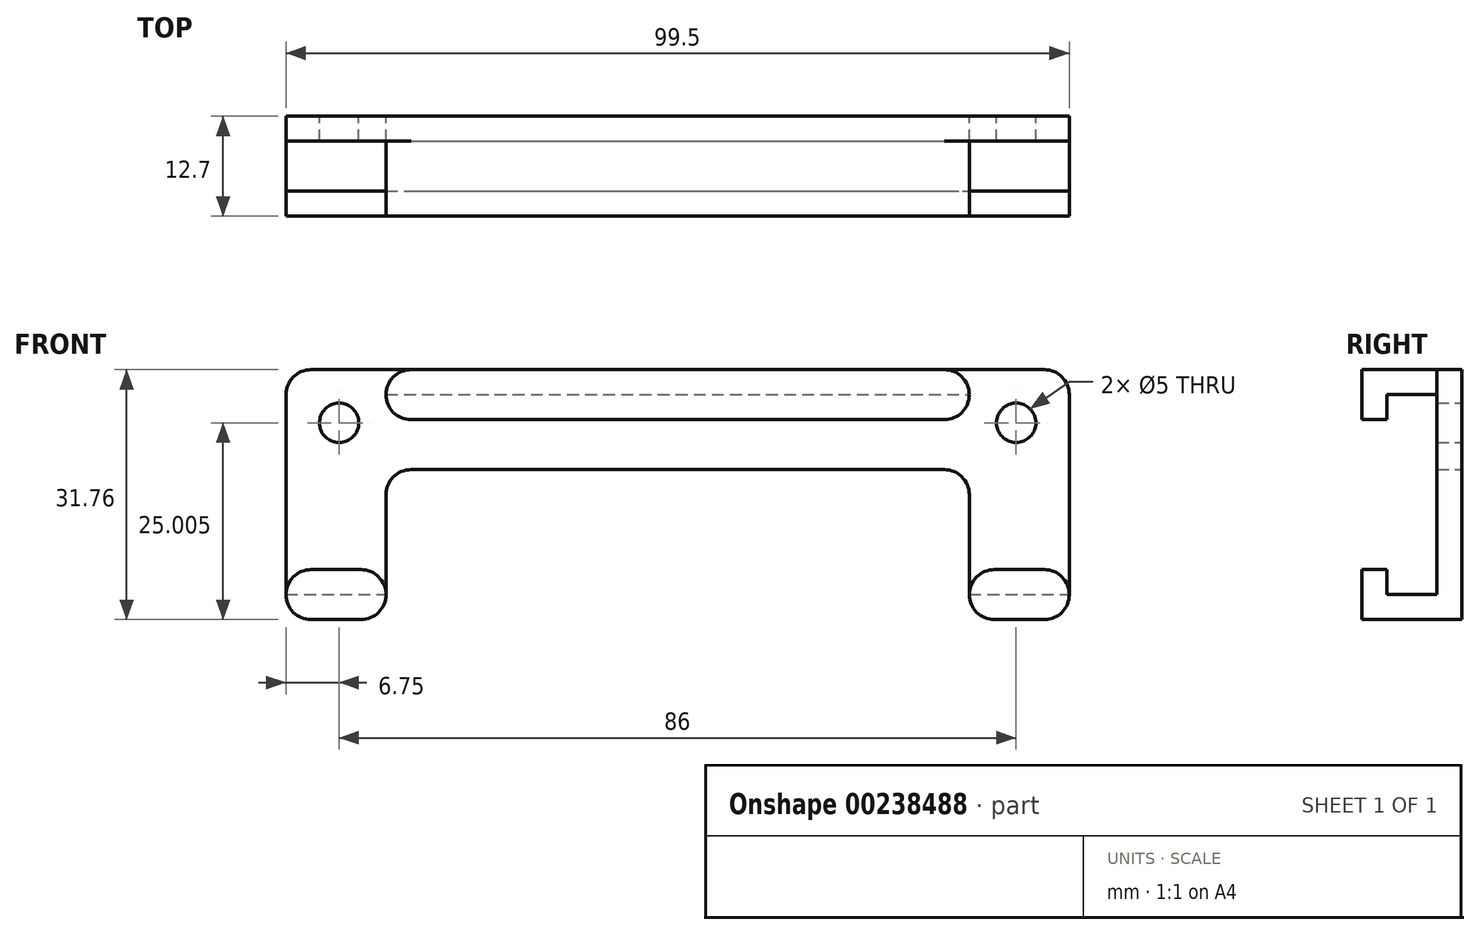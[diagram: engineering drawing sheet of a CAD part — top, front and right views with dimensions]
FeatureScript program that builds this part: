
annotation { "Feature Type Name" : "Feature", "Feature Type Description" : "" }
export const myFeature = defineFeature(function(context is Context, id is Id, definition is map)
    precondition{}
    {
        {
            var Q0;
            Q0=qCreatedBy(makeId("Front.planeOp"),FACE);
            var sketch = newSketch(context, id + "F0", { "sketchPlane" : qUnion([Q0])});
            skLineSegment(sketch, "E0.bottom", {"start": v(49.75, 15.88) * mm, "end": v(-49.75, 15.88) * mm});
            skLineSegment(sketch, "E0.left", {"start": v(49.75, 15.88) * mm, "end": v(49.75, -15.88) * mm});
            skLineSegment(sketch, "E0.right", {"start": v(-49.75, 15.88) * mm, "end": v(-49.75, -15.88) * mm});
            skPoint(sketch, "E0.middle", {"position": v(0, 0) * mm});
            skLineSegment(sketch, "E1.top", {"start": v(-49.75, 9.13) * mm, "end": v(-43, 9.13) * mm, "construction": true});
            skLineSegment(sketch, "E1.right", {"start": v(-43, 15.87) * mm, "end": v(-43, 9.13) * mm, "construction": true});
            skLineSegment(sketch, "E2.top", {"start": v(49.75, 9.13) * mm, "end": v(43, 9.13) * mm, "construction": true});
            skLineSegment(sketch, "E2.right", {"start": v(43, 15.88) * mm, "end": v(43, 9.13) * mm, "construction": true});
            skCircle(sketch, "E3", {"center": v(-43, 9.13) * mm, "radius": 2.5 * mm});
            skCircle(sketch, "E4", {"center": v(43, 9.13) * mm, "radius": 2.5 * mm});
            skLineSegment(sketch, "E5", {"start": v(-37.05, 3.17) * mm, "end": v(37.05, 3.17) * mm});
            skLineSegment(sketch, "E6", {"start": v(37.05, 3.17) * mm, "end": v(37.05, -15.88) * mm});
            skLineSegment(sketch, "E7", {"start": v(-37.05, 3.17) * mm, "end": v(-37.05, -15.88) * mm});
            skLineSegment(sketch, "E8", {"start": v(-37.05, -15.88) * mm, "end": v(-49.75, -15.88) * mm});
            skLineSegment(sketch, "E9", {"start": v(37.05, -15.88) * mm, "end": v(49.75, -15.87) * mm});
            skSolve(sketch);
        }
        {
            var Q0;
            Q0=makeQuery(id+"F0.imprint","IMPRINT",FACE,{"disambiguationData":[TD([[makeQuery(id+"F0.imprint","IMPRINT",EDGE,{"derivedFrom":sQuery(id+"F0.wireOp",EDGE,"E0.bottom")}),1.0]])]});
            extrude(context, id + "F1", {"entities" : qUnion([Q0]), "depth" : 3.17 * mm});
        }
        {
            var Q0;
            Q0=makeQuery(id+"F1.opExtrude","CAP_FACE",FACE,{"disambiguationData":[OSD([sQuery(id+"F0.wireOp",EDGE,"E0.bottom"),sQuery(id+"F0.wireOp",EDGE,"E0.left"),sQuery(id+"F0.wireOp",EDGE,"E0.right"),sQuery(id+"F0.wireOp",EDGE,"E3"),sQuery(id+"F0.wireOp",EDGE,"E4"),sQuery(id+"F0.wireOp",EDGE,"E5"),sQuery(id+"F0.wireOp",EDGE,"E6"),sQuery(id+"F0.wireOp",EDGE,"E7"),sQuery(id+"F0.wireOp",EDGE,"E8"),sQuery(id+"F0.wireOp",EDGE,"E9")])],"isStart":false});
            var sketch = newSketch(context, id + "F2", { "sketchPlane" : qUnion([Q0])});
            skLineSegment(sketch, "E10.bottom", {"start": v(-49.75, -15.88) * mm, "end": v(-37.05, -15.88) * mm});
            skLineSegment(sketch, "E10.top", {"start": v(-49.75, -12.7) * mm, "end": v(-37.05, -12.7) * mm});
            skLineSegment(sketch, "E10.left", {"start": v(-49.75, -15.88) * mm, "end": v(-49.75, -12.7) * mm});
            skLineSegment(sketch, "E10.right", {"start": v(-37.05, -15.88) * mm, "end": v(-37.05, -12.7) * mm});
            skLineSegment(sketch, "E11.bottom", {"start": v(37.05, -15.88) * mm, "end": v(49.75, -15.88) * mm});
            skLineSegment(sketch, "E11.top", {"start": v(37.05, -12.7) * mm, "end": v(49.75, -12.7) * mm});
            skLineSegment(sketch, "E11.left", {"start": v(37.05, -15.88) * mm, "end": v(37.05, -12.7) * mm});
            skLineSegment(sketch, "E11.right", {"start": v(49.75, -15.88) * mm, "end": v(49.75, -12.7) * mm});
            skLineSegment(sketch, "E12.bottom", {"start": v(-49.75, 15.88) * mm, "end": v(49.75, 15.88) * mm});
            skLineSegment(sketch, "E12.left", {"start": v(-49.75, 15.88) * mm, "end": v(-49.75, 12.7) * mm});
            skLineSegment(sketch, "E12.right", {"start": v(49.75, 15.88) * mm, "end": v(49.75, 12.7) * mm});
            skLineSegment(sketch, "E13", {"start": v(-37.05, 3.17) * mm, "end": v(-37.05, 15.88) * mm, "construction": true});
            skLineSegment(sketch, "E14", {"start": v(-49.75, 12.7) * mm, "end": v(-37.05, 12.7) * mm, "construction": true});
            skLineSegment(sketch, "E15", {"start": v(37.05, 3.17) * mm, "end": v(37.05, 15.88) * mm, "construction": true});
            skLineSegment(sketch, "E16", {"start": v(49.75, 12.7) * mm, "end": v(37.05, 12.7) * mm, "construction": true});
            skLineSegment(sketch, "E17.bottom", {"start": v(-37.05, 15.88) * mm, "end": v(37.05, 15.88) * mm});
            skLineSegment(sketch, "E17.top", {"start": v(-37.05, 12.7) * mm, "end": v(37.05, 12.7) * mm});
            skLineSegment(sketch, "E17.left", {"start": v(-37.05, 15.88) * mm, "end": v(-37.05, 12.7) * mm});
            skLineSegment(sketch, "E17.right", {"start": v(37.05, 15.88) * mm, "end": v(37.05, 12.7) * mm});
            skSolve(sketch);
        }
        {
            var Q0;
            Q0 = qSketchRegion(id + "F2", true);
            extrude(context, id + "F3", {"entities" : qUnion([Q0]), "operationType" : NewBodyOperationType.ADD, "depth" : 9.52 * mm});
        }
        {
            var Q0;
            Q0=makeQuery(id+"F3.opExtrude","SWEPT_FACE",FACE,{"disambiguationData":[OSD([sQuery(id+"F2.wireOp",EDGE,"E11.top")])]});
            var sketch = newSketch(context, id + "F4", { "sketchPlane" : qUnion([Q0])});
            skLineSegment(sketch, "E18.bottom", {"start": v(-49.75, -12.7) * mm, "end": v(-37.05, -12.7) * mm});
            skLineSegment(sketch, "E18.top", {"start": v(-49.75, -9.53) * mm, "end": v(-37.05, -9.53) * mm});
            skLineSegment(sketch, "E18.left", {"start": v(-49.75, -12.7) * mm, "end": v(-49.75, -9.53) * mm});
            skLineSegment(sketch, "E18.right", {"start": v(-37.05, -12.7) * mm, "end": v(-37.05, -9.53) * mm});
            skLineSegment(sketch, "E19.bottom", {"start": v(49.75, -12.7) * mm, "end": v(37.05, -12.7) * mm});
            skLineSegment(sketch, "E19.top", {"start": v(49.75, -9.53) * mm, "end": v(37.05, -9.53) * mm});
            skLineSegment(sketch, "E19.left", {"start": v(49.75, -12.7) * mm, "end": v(49.75, -9.53) * mm});
            skLineSegment(sketch, "E19.right", {"start": v(37.05, -12.7) * mm, "end": v(37.05, -9.53) * mm});
            skSolve(sketch);
        }
        {
            var Q0;
            Q0 = qSketchRegion(id + "F4", true);
            extrude(context, id + "F5", {"entities" : qUnion([Q0]), "operationType" : NewBodyOperationType.ADD, "depth" : 3.17 * mm});
        }
        {
            var Q0;
            Q0=makeQuery(id+"F3.opExtrude","SWEPT_FACE",FACE,{"disambiguationData":[OSD([sQuery(id+"F2.wireOp",EDGE,"E17.top")])]});
            var sketch = newSketch(context, id + "F6", { "sketchPlane" : qUnion([Q0])});
            skLineSegment(sketch, "E20.bottom", {"start": v(-37.05, 12.7) * mm, "end": v(37.05, 12.7) * mm});
            skLineSegment(sketch, "E20.top", {"start": v(-37.05, 9.53) * mm, "end": v(37.05, 9.53) * mm});
            skLineSegment(sketch, "E20.left", {"start": v(-37.05, 12.7) * mm, "end": v(-37.05, 9.53) * mm});
            skLineSegment(sketch, "E20.right", {"start": v(37.05, 12.7) * mm, "end": v(37.05, 9.53) * mm});
            skSolve(sketch);
        }
        {
            var Q0;
            Q0 = qSketchRegion(id + "F6", true);
            extrude(context, id + "F7", {"entities" : qUnion([Q0]), "operationType" : NewBodyOperationType.ADD, "depth" : 3.17 * mm});
        }
        {
            var Q0;
            Q0=makeQuery(id+"F1.opExtrude","SWEPT_EDGE",EDGE,{"disambiguationData":[OSD([sQuery(id+"F0.wireOp",EDGE,"E0.bottom"),sQuery(id+"F0.wireOp",EDGE,"E0.right")])]});
            var Q1;
            Q1=makeQuery(id+"F3.boolean.opBoolean","MERGE",EDGE,{"derivedFrom":[makeQuery(id+"F1.opExtrude","SWEPT_EDGE",EDGE,{"disambiguationData":[OSD([sQuery(id+"F0.wireOp",EDGE,"E0.right"),sQuery(id+"F0.wireOp",EDGE,"E8")])]}),makeQuery(id+"F3.opExtrude","SWEPT_EDGE",EDGE,{"disambiguationData":[OSD([sQuery(id+"F2.wireOp",EDGE,"E10.bottom"),sQuery(id+"F2.wireOp",EDGE,"E10.left")])]})]});
            var Q2;
            Q2=makeQuery(id+"F3.boolean.opBoolean","MERGE",EDGE,{"derivedFrom":[makeQuery(id+"F1.opExtrude","SWEPT_EDGE",EDGE,{"disambiguationData":[OSD([sQuery(id+"F0.wireOp",EDGE,"E7"),sQuery(id+"F0.wireOp",EDGE,"E8")])]}),makeQuery(id+"F3.opExtrude","SWEPT_EDGE",EDGE,{"disambiguationData":[OSD([sQuery(id+"F2.wireOp",EDGE,"E10.bottom"),sQuery(id+"F2.wireOp",EDGE,"E10.right")])]})]});
            var Q3;
            Q3=makeQuery(id+"F3.boolean.opBoolean","MERGE",EDGE,{"derivedFrom":[makeQuery(id+"F1.opExtrude","SWEPT_EDGE",EDGE,{"disambiguationData":[OSD([sQuery(id+"F0.wireOp",EDGE,"E0.left"),sQuery(id+"F0.wireOp",EDGE,"E9")])]}),makeQuery(id+"F3.opExtrude","SWEPT_EDGE",EDGE,{"disambiguationData":[OSD([sQuery(id+"F2.wireOp",EDGE,"E11.bottom"),sQuery(id+"F2.wireOp",EDGE,"E11.right")])]})]});
            var Q4;
            Q4=makeQuery(id+"F3.boolean.opBoolean","MERGE",EDGE,{"derivedFrom":[makeQuery(id+"F1.opExtrude","SWEPT_EDGE",EDGE,{"disambiguationData":[OSD([sQuery(id+"F0.wireOp",EDGE,"E6"),sQuery(id+"F0.wireOp",EDGE,"E9")])]}),makeQuery(id+"F3.opExtrude","SWEPT_EDGE",EDGE,{"disambiguationData":[OSD([sQuery(id+"F2.wireOp",EDGE,"E11.bottom"),sQuery(id+"F2.wireOp",EDGE,"E11.left")])]})]});
            var Q5;
            Q5=makeQuery(id+"F1.opExtrude","SWEPT_EDGE",EDGE,{"disambiguationData":[OSD([sQuery(id+"F0.wireOp",EDGE,"E0.bottom"),sQuery(id+"F0.wireOp",EDGE,"E0.left")])]});
            var Q6;
            Q6=makeQuery(id+"F1.opExtrude","SWEPT_EDGE",EDGE,{"disambiguationData":[OSD([sQuery(id+"F0.wireOp",EDGE,"E5"),sQuery(id+"F0.wireOp",EDGE,"E6")])]});
            var Q7;
            Q7=makeQuery(id+"F1.opExtrude","SWEPT_EDGE",EDGE,{"disambiguationData":[OSD([sQuery(id+"F0.wireOp",EDGE,"E5"),sQuery(id+"F0.wireOp",EDGE,"E7")])]});
            var Q8;
            Q8=makeQuery(id+"F5.opExtrude","CAP_EDGE",EDGE,{"disambiguationData":[OSD([sQuery(id+"F4.wireOp",EDGE,"E18.left")])],"isStart":false});
            var Q9;
            Q9=makeQuery(id+"F5.opExtrude","CAP_EDGE",EDGE,{"disambiguationData":[OSD([sQuery(id+"F4.wireOp",EDGE,"E18.right")])],"isStart":false});
            var Q10;
            Q10=makeQuery(id+"F5.opExtrude","CAP_EDGE",EDGE,{"disambiguationData":[OSD([sQuery(id+"F4.wireOp",EDGE,"E19.left")])],"isStart":false});
            var Q11;
            Q11=makeQuery(id+"F5.opExtrude","CAP_EDGE",EDGE,{"disambiguationData":[OSD([sQuery(id+"F4.wireOp",EDGE,"E19.right")])],"isStart":false});
            var Q12;
            Q12=makeQuery(id+"F3.opExtrude","SWEPT_EDGE",EDGE,{"disambiguationData":[OSD([sQuery(id+"F2.wireOp",EDGE,"E12.bottom"),sQuery(id+"F2.wireOp",EDGE,"E17.bottom"),sQuery(id+"F2.wireOp",EDGE,"E17.left")])]});
            var Q13;
            Q13=makeQuery(id+"F7.opExtrude","CAP_EDGE",EDGE,{"disambiguationData":[OSD([sQuery(id+"F6.wireOp",EDGE,"E20.left")])],"isStart":false});
            var Q14;
            Q14=makeQuery(id+"F3.opExtrude","SWEPT_EDGE",EDGE,{"disambiguationData":[OSD([sQuery(id+"F2.wireOp",EDGE,"E12.bottom"),sQuery(id+"F2.wireOp",EDGE,"E17.bottom"),sQuery(id+"F2.wireOp",EDGE,"E17.right")])]});
            var Q15;
            Q15=makeQuery(id+"F7.opExtrude","CAP_EDGE",EDGE,{"disambiguationData":[OSD([sQuery(id+"F6.wireOp",EDGE,"E20.right")])],"isStart":false});
            fillet(context, id + "F8", {"entities" : qUnion([Q0, Q1, Q2, Q3, Q4, Q5, Q6, Q7, Q8, Q9, Q10, Q11, Q12, Q13, Q14, Q15]), "radius" : 3.17 * mm, "tangentPropagation" : true, "allowEdgeOverflow" : false});
        }
    });
